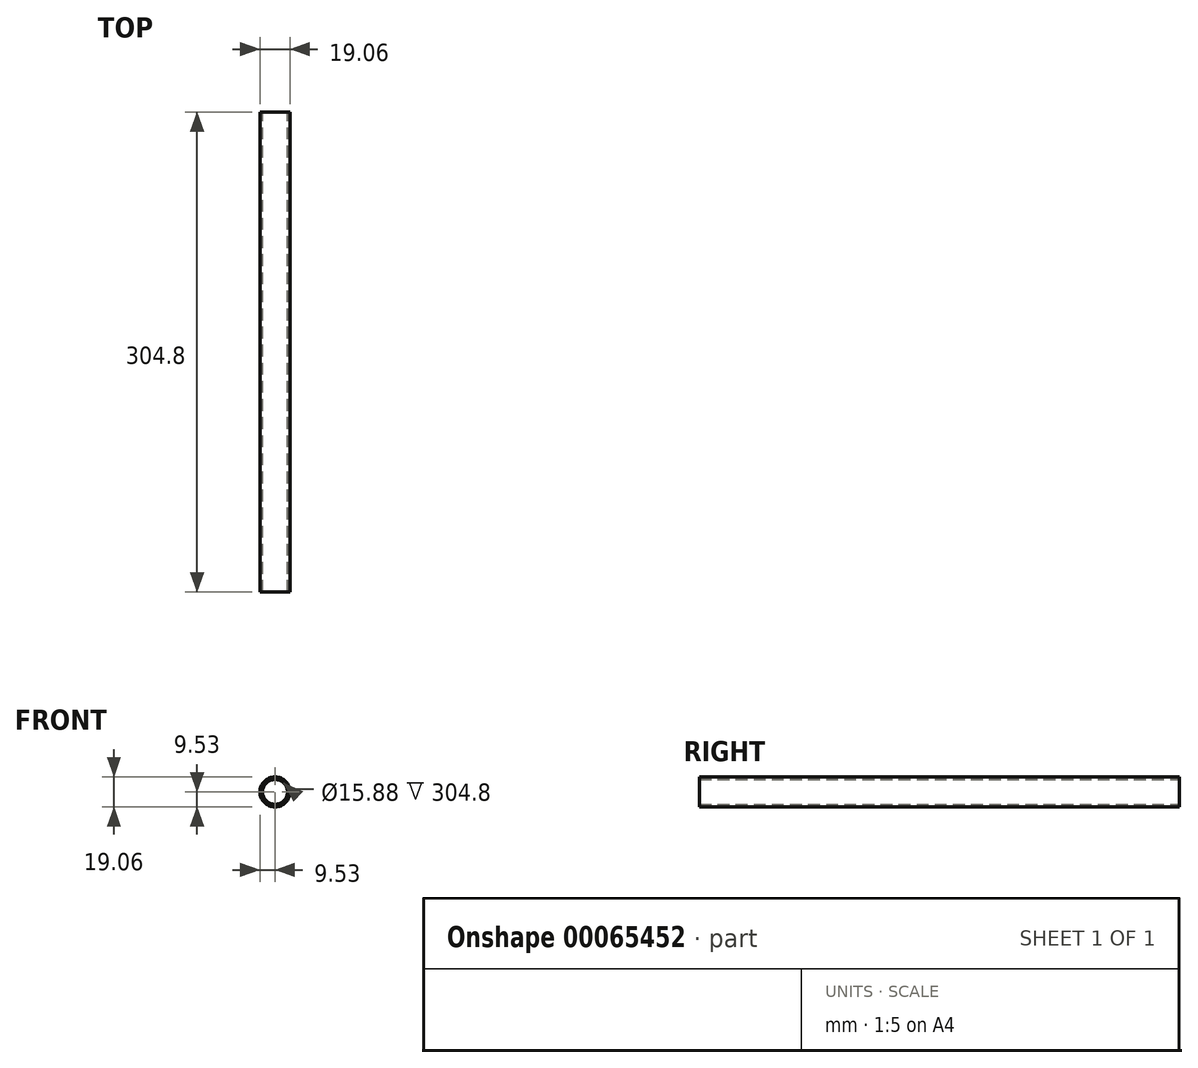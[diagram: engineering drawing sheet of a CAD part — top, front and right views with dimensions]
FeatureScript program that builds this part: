
annotation { "Feature Type Name" : "Feature", "Feature Type Description" : "" }
export const myFeature = defineFeature(function(context is Context, id is Id, definition is map)
    precondition{}
    {
        {
            var Q0;
            Q0=qCreatedBy(makeId("Front.planeOp"),FACE);
            var sketch = newSketch(context, id + "F0", { "sketchPlane" : qUnion([Q0])});
            skCircle(sketch, "E0", {"center": v(0, 0) * mm, "radius": 9.53 * mm});
            skCircle(sketch, "E1", {"center": v(0, 0) * mm, "radius": 7.94 * mm});
            skSolve(sketch);
        }
        {
            var Q0;
            Q0=makeQuery(id+"F0.imprint","IMPRINT",FACE,{"disambiguationData":[TD([[makeQuery(id+"F0.imprint","IMPRINT",EDGE,{"derivedFrom":sQuery(id+"F0.wireOp",EDGE,"E0")}),1.0]])]});
            extrude(context, id + "F1", {"entities" : qUnion([Q0]), "depth" : 304.8 * mm});
        }
    });
